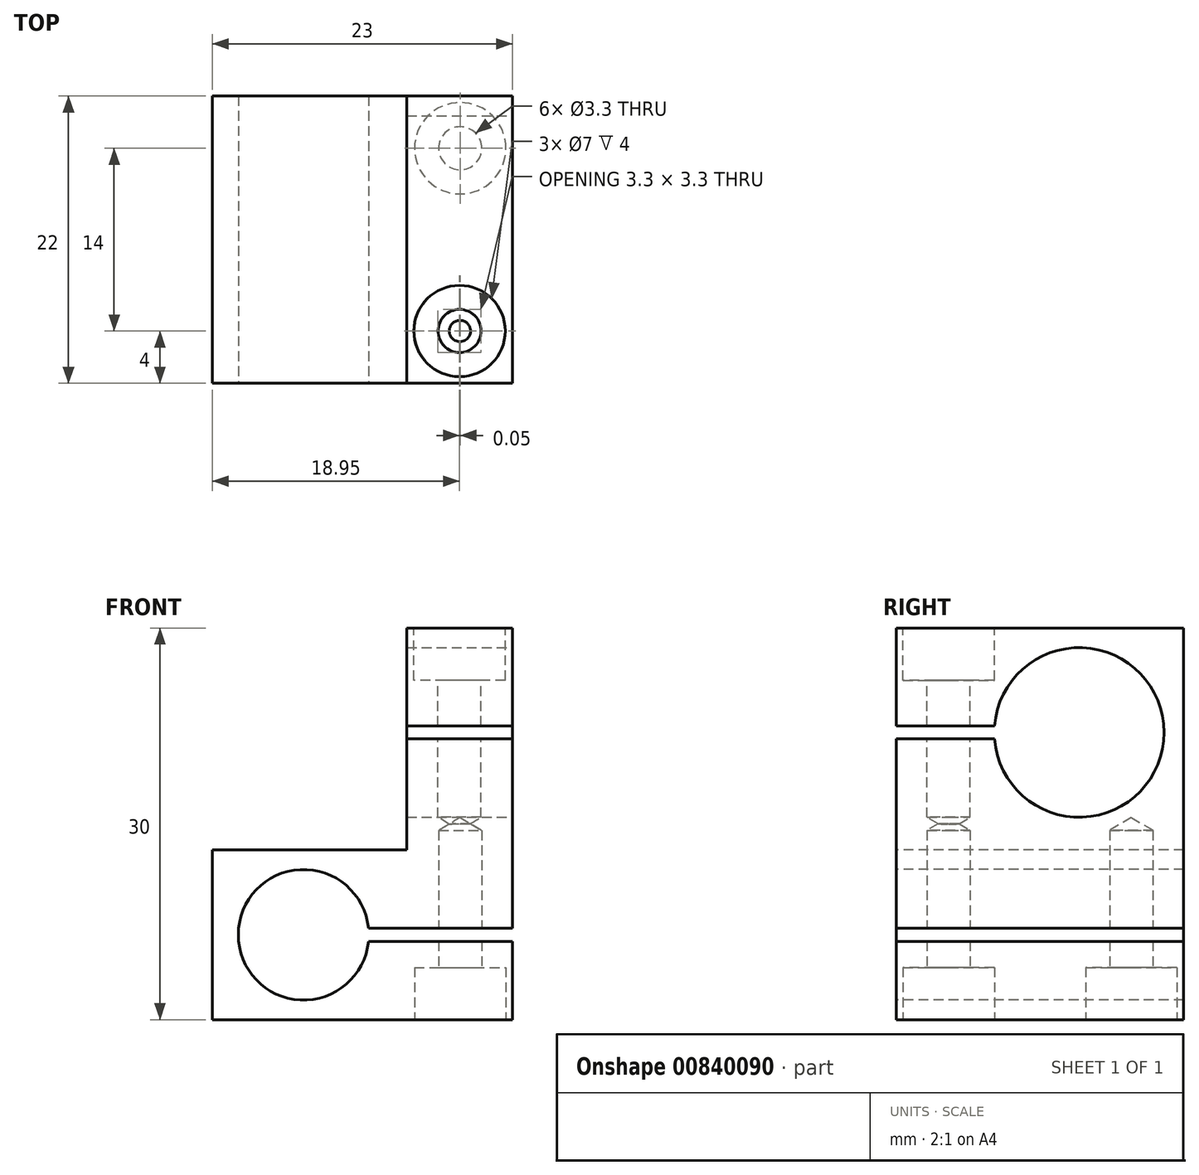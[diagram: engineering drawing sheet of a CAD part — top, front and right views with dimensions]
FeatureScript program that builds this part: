
annotation { "Feature Type Name" : "Feature", "Feature Type Description" : "" }
export const myFeature = defineFeature(function(context is Context, id is Id, definition is map)
    precondition{}
    {
        {
            var Q0;
            Q0=qCreatedBy(makeId("Top.planeOp"),FACE);
            var sketch = newSketch(context, id + "F0", { "sketchPlane" : qUnion([Q0])});
            skLineSegment(sketch, "E0.bottom", {"start": v(-11.5, 11) * mm, "end": v(11.5, 11) * mm});
            skLineSegment(sketch, "E0.top", {"start": v(-11.5, -11) * mm, "end": v(11.5, -11) * mm});
            skLineSegment(sketch, "E0.left", {"start": v(-11.5, 11) * mm, "end": v(-11.5, -11) * mm});
            skLineSegment(sketch, "E0.right", {"start": v(11.5, 11) * mm, "end": v(11.5, -11) * mm});
            skPoint(sketch, "E0.middle", {"position": v(0, 0) * mm});
            skSolve(sketch);
        }
        {
            var Q0;
            Q0 = qSketchRegion(id + "F0", true);
            extrude(context, id + "F1", {"entities" : qUnion([Q0]), "depth" : 13 * mm, "offsetDistance" : 25 * mm});
        }
        {
            var Q0;
            Q0=makeQuery(id+"F1.opExtrude","CAP_FACE",FACE,{"disambiguationData":[OSD([sQuery(id+"F0.wireOp",EDGE,"E0.bottom"),sQuery(id+"F0.wireOp",EDGE,"E0.top"),sQuery(id+"F0.wireOp",EDGE,"E0.left"),sQuery(id+"F0.wireOp",EDGE,"E0.right")])],"isStart":false});
            var sketch = newSketch(context, id + "F2", { "sketchPlane" : qUnion([Q0])});
            skLineSegment(sketch, "E1.bottom", {"start": v(11.5, 11) * mm, "end": v(3.4, 11) * mm});
            skLineSegment(sketch, "E1.top", {"start": v(11.5, -11) * mm, "end": v(3.4, -11) * mm});
            skLineSegment(sketch, "E1.left", {"start": v(11.5, 11) * mm, "end": v(11.5, -11) * mm});
            skLineSegment(sketch, "E1.right", {"start": v(3.4, 11) * mm, "end": v(3.4, -11) * mm});
            skSolve(sketch);
        }
        {
            var Q0;
            Q0 = qSketchRegion(id + "F2", true);
            extrude(context, id + "F3", {"entities" : qUnion([Q0]), "operationType" : NewBodyOperationType.ADD, "depth" : 17 * mm, "offsetDistance" : 25 * mm});
        }
        {
            var Q0;
            Q0=makeQuery(id+"F3.boolean.opBoolean","MERGE",FACE,{"derivedFrom":[makeQuery(id+"F1.opExtrude","SWEPT_FACE",FACE,{"disambiguationData":[OSD([sQuery(id+"F0.wireOp",EDGE,"E0.top")])]}),makeQuery(id+"F3.opExtrude","SWEPT_FACE",FACE,{"disambiguationData":[OSD([sQuery(id+"F2.wireOp",EDGE,"E1.top")])]})]});
            var sketch = newSketch(context, id + "F4", { "sketchPlane" : qUnion([Q0])});
            skLineSegment(sketch, "E2", {"start": v(-11.5, 6.5) * mm, "end": v(-4.5, 6.5) * mm});
            skCircle(sketch, "E3", {"center": v(-4.5, 6.5) * mm, "radius": 5 * mm});
            skSolve(sketch);
        }
        {
            var Q0;
            Q0 = qSketchRegion(id + "F4", true);
            extrude(context, id + "F5", {"entities" : qUnion([Q0]), "operationType" : NewBodyOperationType.REMOVE, "oppositeDirection" : true, "depth" : 30 * mm, "offsetDistance" : 25 * mm});
        }
        {
            var Q0;
            Q0=makeQuery(id+"F3.boolean.opBoolean","MERGE",FACE,{"derivedFrom":[makeQuery(id+"F1.opExtrude","SWEPT_FACE",FACE,{"disambiguationData":[OSD([sQuery(id+"F0.wireOp",EDGE,"E0.right")])]}),makeQuery(id+"F3.opExtrude","SWEPT_FACE",FACE,{"disambiguationData":[OSD([sQuery(id+"F2.wireOp",EDGE,"E1.left")])]})]});
            var sketch = newSketch(context, id + "F6", { "sketchPlane" : qUnion([Q0])});
            skLineSegment(sketch, "E4", {"start": v(11, 22) * mm, "end": v(3, 22) * mm});
            skCircle(sketch, "E5", {"center": v(3, 22) * mm, "radius": 6.5 * mm});
            skLineSegment(sketch, "E6", {"start": v(3, 22) * mm, "end": v(-15.59, 22) * mm});
            skLineSegment(sketch, "E7.bottom", {"start": v(-15.59, 22.5) * mm, "end": v(3, 22.5) * mm});
            skLineSegment(sketch, "E7.top", {"start": v(-15.59, 21.5) * mm, "end": v(3, 21.5) * mm});
            skLineSegment(sketch, "E7.left", {"start": v(-15.59, 22.5) * mm, "end": v(-15.59, 21.5) * mm});
            skLineSegment(sketch, "E7.right", {"start": v(3, 22.5) * mm, "end": v(3, 21.5) * mm});
            skPoint(sketch, "E7.middle", {"position": v(-6.3, 22) * mm});
            skSolve(sketch);
        }
        {
            var Q0;
            Q0 = qSketchRegion(id + "F6", true);
            extrude(context, id + "F7", {"entities" : qUnion([Q0]), "operationType" : NewBodyOperationType.REMOVE, "oppositeDirection" : true, "depth" : 25 * mm, "offsetDistance" : 25 * mm});
        }
        {
            var Q0;
            Q0=makeQuery(id+"F3.boolean.opBoolean","MERGE",FACE,{"derivedFrom":[makeQuery(id+"F1.opExtrude","SWEPT_FACE",FACE,{"disambiguationData":[OSD([sQuery(id+"F0.wireOp",EDGE,"E0.top")])]}),makeQuery(id+"F3.opExtrude","SWEPT_FACE",FACE,{"disambiguationData":[OSD([sQuery(id+"F2.wireOp",EDGE,"E1.top")])]})]});
            var sketch = newSketch(context, id + "F8", { "sketchPlane" : qUnion([Q0])});
            skLineSegment(sketch, "E8", {"start": v(-11.5, 6.5) * mm, "end": v(25.66, 6.5) * mm});
            skLineSegment(sketch, "E9.bottom", {"start": v(-4.05, 7) * mm, "end": v(27.05, 7) * mm});
            skLineSegment(sketch, "E9.top", {"start": v(-4.05, 6) * mm, "end": v(27.05, 6) * mm});
            skLineSegment(sketch, "E9.left", {"start": v(-4.05, 7) * mm, "end": v(-4.05, 6) * mm});
            skLineSegment(sketch, "E9.right", {"start": v(27.05, 7) * mm, "end": v(27.05, 6) * mm});
            skPoint(sketch, "E9.middle", {"position": v(11.5, 6.5) * mm});
            skPoint(sketch, "E9.cornerSnap0", {"position": v(-4.05, 13) * mm});
            skSolve(sketch);
        }
        {
            var Q0;
            Q0 = qSketchRegion(id + "F8", true);
            extrude(context, id + "F9", {"entities" : qUnion([Q0]), "operationType" : NewBodyOperationType.REMOVE, "oppositeDirection" : true, "depth" : 45 * mm, "offsetDistance" : 25 * mm});
        }
        {
            var Q0;
            Q0 = qSketchRegion(id + "F6", true);
            extrude(context, id + "F10", {"entities" : qUnion([Q0]), "operationType" : NewBodyOperationType.REMOVE, "oppositeDirection" : true, "depth" : 40 * mm, "offsetDistance" : 25 * mm});
        }
        {
            var Q0;
            Q0=makeQuery(id+"F3.opExtrude","CAP_FACE",FACE,{"disambiguationData":[OSD([sQuery(id+"F2.wireOp",EDGE,"E1.bottom"),sQuery(id+"F2.wireOp",EDGE,"E1.top"),sQuery(id+"F2.wireOp",EDGE,"E1.left"),sQuery(id+"F2.wireOp",EDGE,"E1.right")])],"isStart":false});
            var sketch = newSketch(context, id + "F11", { "sketchPlane" : qUnion([Q0])});
            skLineSegment(sketch, "E10", {"start": v(7.45, -11) * mm, "end": v(7.45, -7) * mm});
            skCircle(sketch, "E11", {"center": v(7.45, -7) * mm, "radius": 3.44 * mm});
            skSolve(sketch);
        }
        {
            var Q0;
            Q0=sQuery(id+"F11.wireOp",VERTEX,"E10.end");
            var Q1;
            Q1=makeQuery(id+"F1.opExtrude","SWEPT_BODY",BODY,{"disambiguationData":[OSD([sQuery(id+"F0.wireOp",EDGE,"E0.bottom"),sQuery(id+"F0.wireOp",EDGE,"E0.top"),sQuery(id+"F0.wireOp",EDGE,"E0.left"),sQuery(id+"F0.wireOp",EDGE,"E0.right")])]});
            hole(context, id + "F12", {"style" : HoleStyle.C_BORE, "endStyle" : HoleEndStyle.BLIND, "holeDiameter" : 3.3 * mm, "cBoreDiameter" : 7 * mm, "cBoreDepth" : 4 * mm, "majorDiameter" : 4 * mm, "holeDepth" : 14.5 * mm, "isTappedThrough" : true, "tappedDepth" : 12.4 * mm, "tapClearance" : 3, "locations" : qUnion([Q0]), "scope" : qUnion([Q1])});
        }
        {
            var Q0;
            Q0 = qSketchRegion(id + "F11", true);
            extrude(context, id + "F13", {"entities" : qUnion([Q0]), "operationType" : NewBodyOperationType.REMOVE, "oppositeDirection" : true, "depth" : 3.05 * mm, "offsetDistance" : 25 * mm});
        }
        {
            var Q0;
            Q0=makeQuery(id+"F1.opExtrude","CAP_FACE",FACE,{"disambiguationData":[OSD([sQuery(id+"F0.wireOp",EDGE,"E0.bottom"),sQuery(id+"F0.wireOp",EDGE,"E0.top"),sQuery(id+"F0.wireOp",EDGE,"E0.left"),sQuery(id+"F0.wireOp",EDGE,"E0.right")])],"isStart":true});
            var sketch = newSketch(context, id + "F14", { "sketchPlane" : qUnion([Q0])});
            skLineSegment(sketch, "E12", {"start": v(11.5, 7) * mm, "end": v(7.5, 7) * mm});
            skLineSegment(sketch, "E13", {"start": v(7.5, 7) * mm, "end": v(7.5, 11) * mm});
            skLineSegment(sketch, "E14", {"start": v(7.5, -11) * mm, "end": v(7.5, -7) * mm});
            skLineSegment(sketch, "E15", {"start": v(7.5, -7) * mm, "end": v(11.5, -7) * mm});
            skCircle(sketch, "E16", {"center": v(7.5, 7) * mm, "radius": 3.44 * mm});
            skCircle(sketch, "E17", {"center": v(7.5, -7) * mm, "radius": 3.44 * mm});
            skSolve(sketch);
        }
        {
            var Q0;
            Q0=sQuery(id+"F14.wireOp",VERTEX,"E12.end");
            var Q1;
            Q1=sQuery(id+"F14.wireOp",VERTEX,"E14.end");
            var Q2;
            Q2=makeQuery(id+"F1.opExtrude","SWEPT_BODY",BODY,{"disambiguationData":[OSD([sQuery(id+"F0.wireOp",EDGE,"E0.bottom"),sQuery(id+"F0.wireOp",EDGE,"E0.top"),sQuery(id+"F0.wireOp",EDGE,"E0.left"),sQuery(id+"F0.wireOp",EDGE,"E0.right")])]});
            hole(context, id + "F15", {"style" : HoleStyle.C_BORE, "endStyle" : HoleEndStyle.BLIND, "holeDiameter" : 3.3 * mm, "cBoreDiameter" : 7 * mm, "cBoreDepth" : 4 * mm, "majorDiameter" : 4 * mm, "holeDepth" : 14.5 * mm, "isTappedThrough" : true, "tappedDepth" : 12.4 * mm, "tapClearance" : 3, "locations" : qUnion([Q0, Q1]), "scope" : qUnion([Q2])});
        }
        {
            var Q0;
            Q0 = qSketchRegion(id + "F14", true);
            extrude(context, id + "F16", {"entities" : qUnion([Q0]), "operationType" : NewBodyOperationType.REMOVE, "oppositeDirection" : true, "depth" : 3.05 * mm, "offsetDistance" : 25 * mm});
        }
    });
